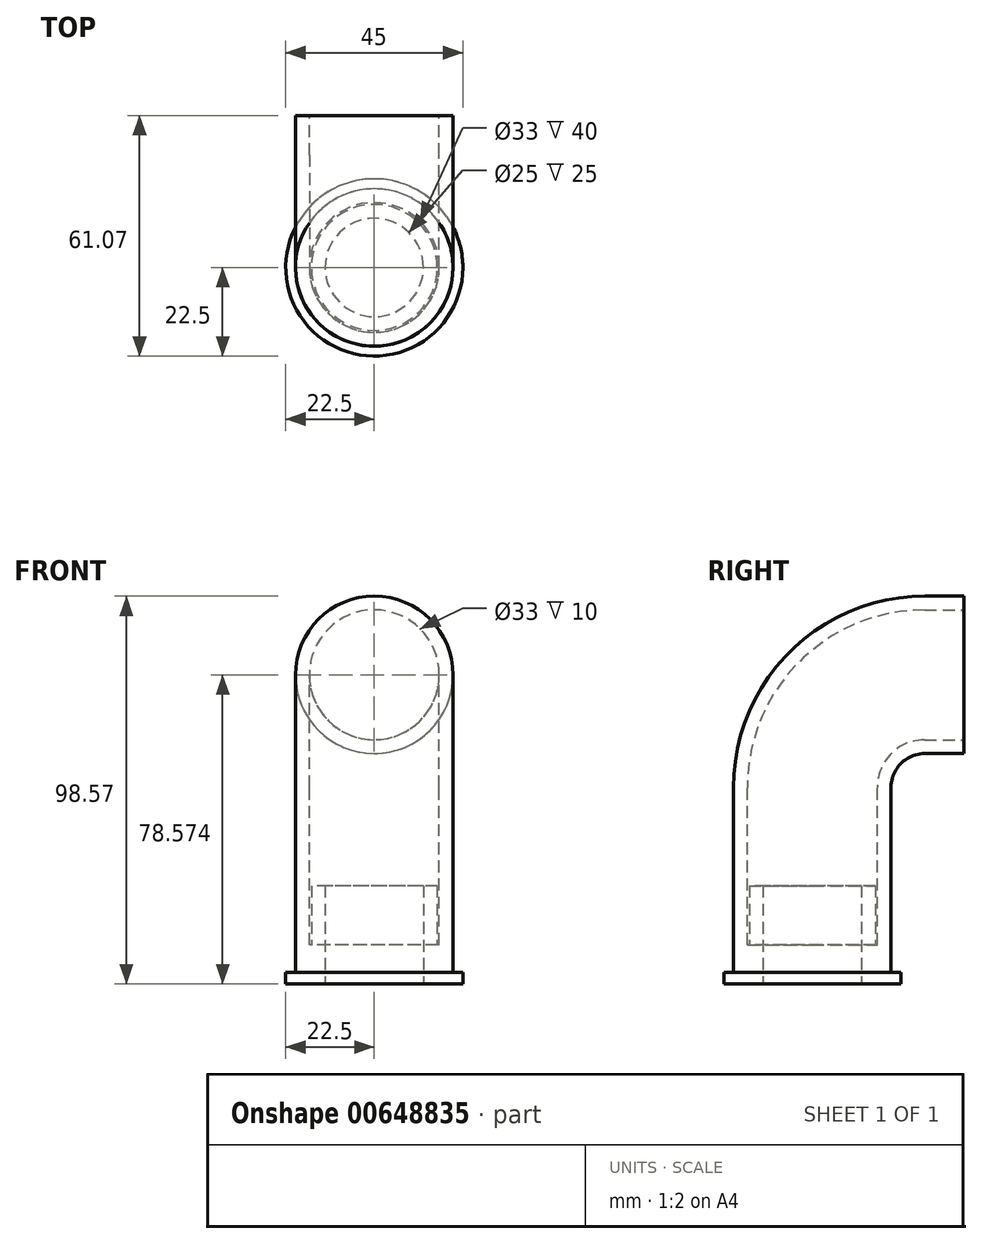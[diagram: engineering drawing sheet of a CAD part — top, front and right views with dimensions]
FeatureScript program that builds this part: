
annotation { "Feature Type Name" : "Feature", "Feature Type Description" : "" }
export const myFeature = defineFeature(function(context is Context, id is Id, definition is map)
    precondition{}
    {
        {
            var Q0;
            Q0=qCreatedBy(makeId("Top.planeOp"),FACE);
            var sketch = newSketch(context, id + "F0", { "sketchPlane" : qUnion([Q0])});
            skCircle(sketch, "E0", {"center": v(0, 0) * mm, "radius": 20 * mm});
            skCircle(sketch, "E1", {"center": v(0, 0) * mm, "radius": 16.5 * mm});
            skSolve(sketch);
        }
        {
            var Q0;
            Q0=qCreatedBy(makeId("Right.planeOp"),FACE);
            var sketch = newSketch(context, id + "F1", { "sketchPlane" : qUnion([Q0])});
            skLineSegment(sketch, "E2", {"start": v(0, 0) * mm, "end": v(0, 50) * mm});
            skLineSegment(sketch, "E3.0", {"start": v(-20, 0) * mm, "end": v(20, 0) * mm, "construction": true});
            skArc(sketch, "E4", {"start": v(28.57, 78.57) * mm, "mid": v(8.37, 70.2) * mm, "end": v(0, 50) * mm});
            skLineSegment(sketch, "E5", {"start": v(28.57, 78.57) * mm, "end": v(38.57, 78.57) * mm});
            skSolve(sketch);
        }
        {
            var Q0;
            Q0=qSketchRegion(id+"F0",true);
            var Q1;
            Q1=sQuery(id+"F1.wireOp",EDGE,"E5");
            var Q2;
            Q2=sQuery(id+"F1.wireOp",EDGE,"E4");
            var Q3;
            Q3=sQuery(id+"F1.wireOp",EDGE,"E2");
            sweep(context, id + "F2", {"profiles" : qUnion([Q0]), "path" : qUnion([Q1, Q2, Q3])});
        }
        {
            var Q0;
            Q0=qCreatedBy(makeId("Top.planeOp"),FACE);
            var sketch = newSketch(context, id + "F3", { "sketchPlane" : qUnion([Q0])});
            skCircle(sketch, "E6.0", {"center": v(0, 0) * mm, "radius": 20 * mm});
            skCircle(sketch, "E7", {"center": v(0, 0) * mm, "radius": 16 * mm, "construction": true});
            skCircle(sketch, "E8", {"center": v(0, 0) * mm, "radius": 12.5 * mm});
            skSolve(sketch);
        }
        {
            var Q0;
            Q0 = qSketchRegion(id + "F3", true);
            var Q1;
            Q1=sQuery(id+"F3.wireOp",EDGE,"E6.0");
            var Q2;
            Q2=sQuery(id+"F3.wireOp",EDGE,"E8");
            extrude(context, id + "F4", {"entities" : qUnion([Q0]), "surfaceEntities" : qUnion([Q1, Q2]), "depth" : 10 * mm, "offsetDistance" : 25 * mm});
        }
        {
            var Q0;
            Q0=makeQuery(id+"F4.opExtrude","CAP_FACE",FACE,{"disambiguationData":[OSD([sQuery(id+"F3.wireOp",EDGE,"E6.0"),sQuery(id+"F3.wireOp",EDGE,"E8")])],"isStart":false});
            var sketch = newSketch(context, id + "F5", { "sketchPlane" : qUnion([Q0])});
            skCircle(sketch, "E9.0", {"center": v(0, 0) * mm, "radius": 12.5 * mm});
            skCircle(sketch, "E10.0", {"center": v(0, 0) * mm, "radius": 16 * mm});
            skSolve(sketch);
        }
        {
            var Q0;
            Q0 = qSketchRegion(id + "F5", true);
            extrude(context, id + "F6", {"entities" : qUnion([Q0]), "operationType" : NewBodyOperationType.ADD, "depth" : 15 * mm, "offsetDistance" : 25 * mm});
        }
        {
            var Q0;
            Q0=qCreatedBy(makeId("Top.planeOp"),FACE);
            var sketch = newSketch(context, id + "F7", { "sketchPlane" : qUnion([Q0])});
            skCircle(sketch, "E11.0", {"center": v(0, 0) * mm, "radius": 20 * mm});
            skCircle(sketch, "E12", {"center": v(0, 0) * mm, "radius": 22.5 * mm});
            skSolve(sketch);
        }
        {
            var Q0;
            Q0 = qSketchRegion(id + "F7", true);
            extrude(context, id + "F8", {"entities" : qUnion([Q0]), "operationType" : NewBodyOperationType.ADD, "depth" : 3 * mm, "offsetDistance" : 25 * mm});
        }
    });
